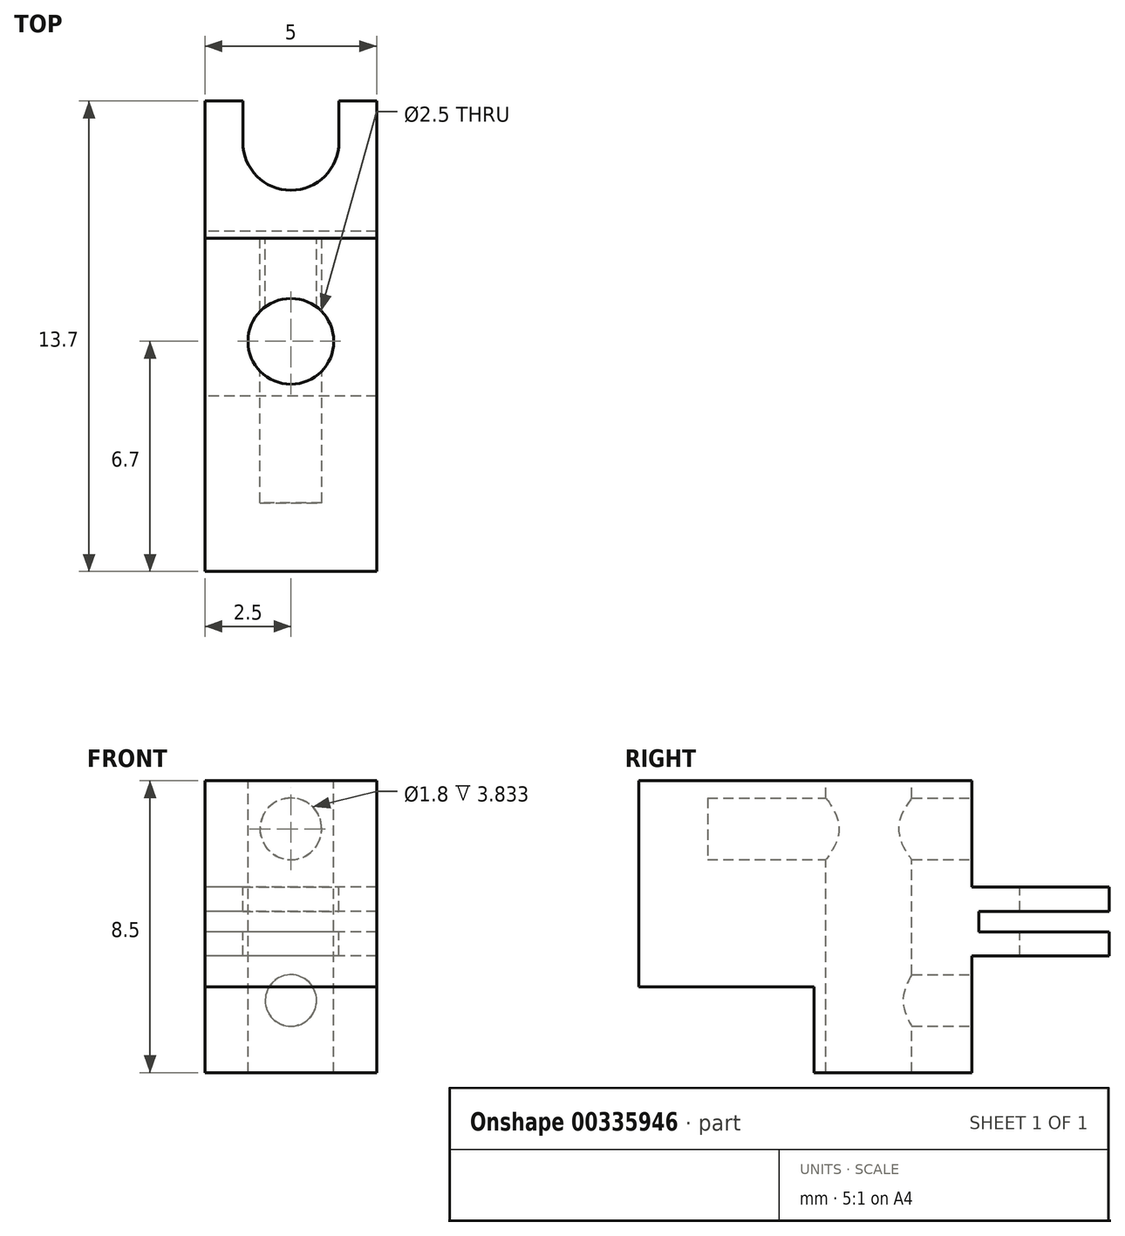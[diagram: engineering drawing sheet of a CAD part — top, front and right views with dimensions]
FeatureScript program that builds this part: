
annotation { "Feature Type Name" : "Feature", "Feature Type Description" : "" }
export const myFeature = defineFeature(function(context is Context, id is Id, definition is map)
    precondition{}
    {
        {
            var Q0;
            Q0=qCreatedBy(makeId("Right.planeOp"),FACE);
            var sketch = newSketch(context, id + "F0", { "sketchPlane" : qUnion([Q0])});
            skLineSegment(sketch, "E0", {"start": v(0, 0) * mm, "end": v(9.7, 0) * mm});
            skLineSegment(sketch, "E1", {"start": v(9.7, 0) * mm, "end": v(9.7, -3.1) * mm});
            skLineSegment(sketch, "E2", {"start": v(9.7, -3.1) * mm, "end": v(13.7, -3.1) * mm});
            skLineSegment(sketch, "E3", {"start": v(13.7, -4.4) * mm, "end": v(9.9, -4.4) * mm});
            skLineSegment(sketch, "E4", {"start": v(9.9, -3.8) * mm, "end": v(9.9, -4.4) * mm});
            skLineSegment(sketch, "E5", {"start": v(9.9, -3.8) * mm, "end": v(13.7, -3.8) * mm});
            skLineSegment(sketch, "E6", {"start": v(13.7, -5.1) * mm, "end": v(9.7, -5.1) * mm});
            skLineSegment(sketch, "E7", {"start": v(9.7, -5.1) * mm, "end": v(9.7, -8.5) * mm});
            skLineSegment(sketch, "E8", {"start": v(9.7, -8.5) * mm, "end": v(5.1, -8.5) * mm});
            skLineSegment(sketch, "E9", {"start": v(5.1, -8.5) * mm, "end": v(5.1, -6) * mm});
            skLineSegment(sketch, "E10", {"start": v(5.1, -6) * mm, "end": v(0, -6) * mm});
            skLineSegment(sketch, "E11", {"start": v(0, -6) * mm, "end": v(0, 0) * mm});
            skPoint(sketch, "E12", {"position": v(9.9, -3.8) * mm});
            skPoint(sketch, "E13", {"position": v(9.9, -4.1) * mm});
            skLineSegment(sketch, "E14", {"start": v(13.7, -3.1) * mm, "end": v(13.7, -3.8) * mm});
            skLineSegment(sketch, "E15", {"start": v(13.7, -4.4) * mm, "end": v(13.7, -5.1) * mm});
            skSolve(sketch);
        }
        {
            var Q0;
            Q0 = qSketchRegion(id + "F0", true);
            extrude(context, id + "F1", {"entities" : qUnion([Q0]), "depth" : 5 * mm});
        }
        {
            var Q0;
            Q0=makeQuery(id+"F1.opExtrude","SWEPT_FACE",FACE,{"disambiguationData":[OSD([sQuery(id+"F0.wireOp",EDGE,"E2")])]});
            var sketch = newSketch(context, id + "F2", { "sketchPlane" : qUnion([Q0])});
            skLineSegment(sketch, "E16.0", {"start": v(5, 13.7) * mm, "end": v(0, 13.7) * mm, "construction": true});
            skPoint(sketch, "E17", {"position": v(2.5, 13.7) * mm});
            skLineSegment(sketch, "E18", {"start": v(2.5, 13.7) * mm, "end": v(2.5, 12.5) * mm, "construction": true});
            skArc(sketch, "E19", {"start": v(1.1, 12.5) * mm, "mid": v(2.5, 11.1) * mm, "end": v(3.9, 12.5) * mm});
            skLineSegment(sketch, "E20", {"start": v(1.1, 12.5) * mm, "end": v(1.1, 13.7) * mm});
            skLineSegment(sketch, "E21", {"start": v(1.1, 13.7) * mm, "end": v(3.9, 13.7) * mm});
            skLineSegment(sketch, "E22", {"start": v(3.9, 13.7) * mm, "end": v(3.9, 12.5) * mm});
            skPoint(sketch, "E23", {"position": v(2.5, 11.1) * mm});
            skSolve(sketch);
        }
        {
            var Q0;
            Q0 = qSketchRegion(id + "F2", true);
            extrude(context, id + "F3", {"entities" : qUnion([Q0]), "operationType" : NewBodyOperationType.REMOVE, "endBound" : BoundingType.THROUGH_ALL, "oppositeDirection" : true, "depth" : 25 * mm});
        }
        {
            var Q0;
            Q0=makeQuery(id+"F1.opExtrude","SWEPT_FACE",FACE,{"disambiguationData":[OSD([sQuery(id+"F0.wireOp",EDGE,"E0")])]});
            var sketch = newSketch(context, id + "F4", { "sketchPlane" : qUnion([Q0])});
            skCircle(sketch, "E24", {"center": v(2.5, 6.7) * mm, "radius": 1.25 * mm});
            skPoint(sketch, "E25.endSnap0", {"position": v(5, 4.85) * mm});
            skLineSegment(sketch, "E26", {"start": v(0, 6.7) * mm, "end": v(5, 6.7) * mm, "construction": true});
            skLineSegment(sketch, "E27.0", {"start": v(5, 9.7) * mm, "end": v(0, 9.7) * mm, "construction": true});
            skSolve(sketch);
        }
        {
            var Q0;
            Q0 = qSketchRegion(id + "F4", true);
            extrude(context, id + "F5", {"entities" : qUnion([Q0]), "operationType" : NewBodyOperationType.REMOVE, "endBound" : BoundingType.THROUGH_ALL, "oppositeDirection" : true, "depth" : 25 * mm});
        }
        {
            var Q0;
            Q0=makeQuery(id+"F1.opExtrude","SWEPT_FACE",FACE,{"disambiguationData":[OSD([sQuery(id+"F0.wireOp",EDGE,"E1")])]});
            var sketch = newSketch(context, id + "F6", { "sketchPlane" : qUnion([Q0])});
            skLineSegment(sketch, "E28.0", {"start": v(-5, 0) * mm, "end": v(0, 0) * mm, "construction": true});
            skPoint(sketch, "E29", {"position": v(-2.5, 0) * mm});
            skLineSegment(sketch, "E30", {"start": v(-2.5, 0) * mm, "end": v(-2.5, -1.4) * mm, "construction": true});
            skCircle(sketch, "E31", {"center": v(-2.5, -1.4) * mm, "radius": 0.9 * mm});
            skSolve(sketch);
        }
        {
            var Q0;
            Q0 = qSketchRegion(id + "F6", true);
            extrude(context, id + "F7", {"entities" : qUnion([Q0]), "operationType" : NewBodyOperationType.REMOVE, "oppositeDirection" : true, "depth" : 7.7 * mm});
        }
        {
            var Q0;
            Q0=makeQuery(id+"F1.opExtrude","SWEPT_FACE",FACE,{"disambiguationData":[OSD([sQuery(id+"F0.wireOp",EDGE,"E7")])]});
            var sketch = newSketch(context, id + "F8", { "sketchPlane" : qUnion([Q0])});
            skCircle(sketch, "E32.0", {"center": v(-2.5, -1.4) * mm, "radius": 0.9 * mm, "construction": true});
            skLineSegment(sketch, "E33", {"start": v(-2.5, -1.4) * mm, "end": v(-2.5, -6.4) * mm, "construction": true});
            skCircle(sketch, "E34", {"center": v(-2.5, -6.4) * mm, "radius": 0.75 * mm});
            skSolve(sketch);
        }
        {
            var Q0;
            Q0 = qSketchRegion(id + "F8", true);
            extrude(context, id + "F9", {"entities" : qUnion([Q0]), "operationType" : NewBodyOperationType.REMOVE, "endBound" : BoundingType.UP_TO_NEXT, "oppositeDirection" : true, "depth" : 25 * mm});
        }
    });
